# Revit family: QF_GIORIK_CPE946
name_source: partatom
category: Specialty Equipment
revit_build: Autodesk Revit 2014 (Build: 20140709_2115(x64)
units: mm (PartAtom-declared; Revit-internal decimal feet)

## types (1)
- CPE946
    Apparent Power = 18000 VA
    Assembly Code = E1090320
    Cold Water Maximum Pressure = 50000.0 Pa
    Cold Water Minimum Pressure = 20000.0 Pa
    Cold Water Size = 1/2"
    Cold Water Temperature Recommended = 0 °C
    Cycle = 50 Hz
    Description = 40+40 LITRE TWIN TANK ELECTRIC PASTA COOKER.
    FL Amps = 0 A
    HP = 24.138360000000
    Indirect Waste Flow = 0.0 L/s
    Indirect Waste Size = 1"
    Manufacturer = GIORIK
    Max Overcurrent Protection = 0 A
    Min Ckt Ampacity = 0 A
    Model = CPE946
    Phase = 3
    URL = www.giorik.com
    URL Cutsheet = www.giorik.com
    Volts = 400 V
    Watts = 18000 W
    Weight in Pounds = 220.462

## geometry (parser evidence)
native form markers: Blend x14, Sweep x3
no freeform markers — native parametric forms only
